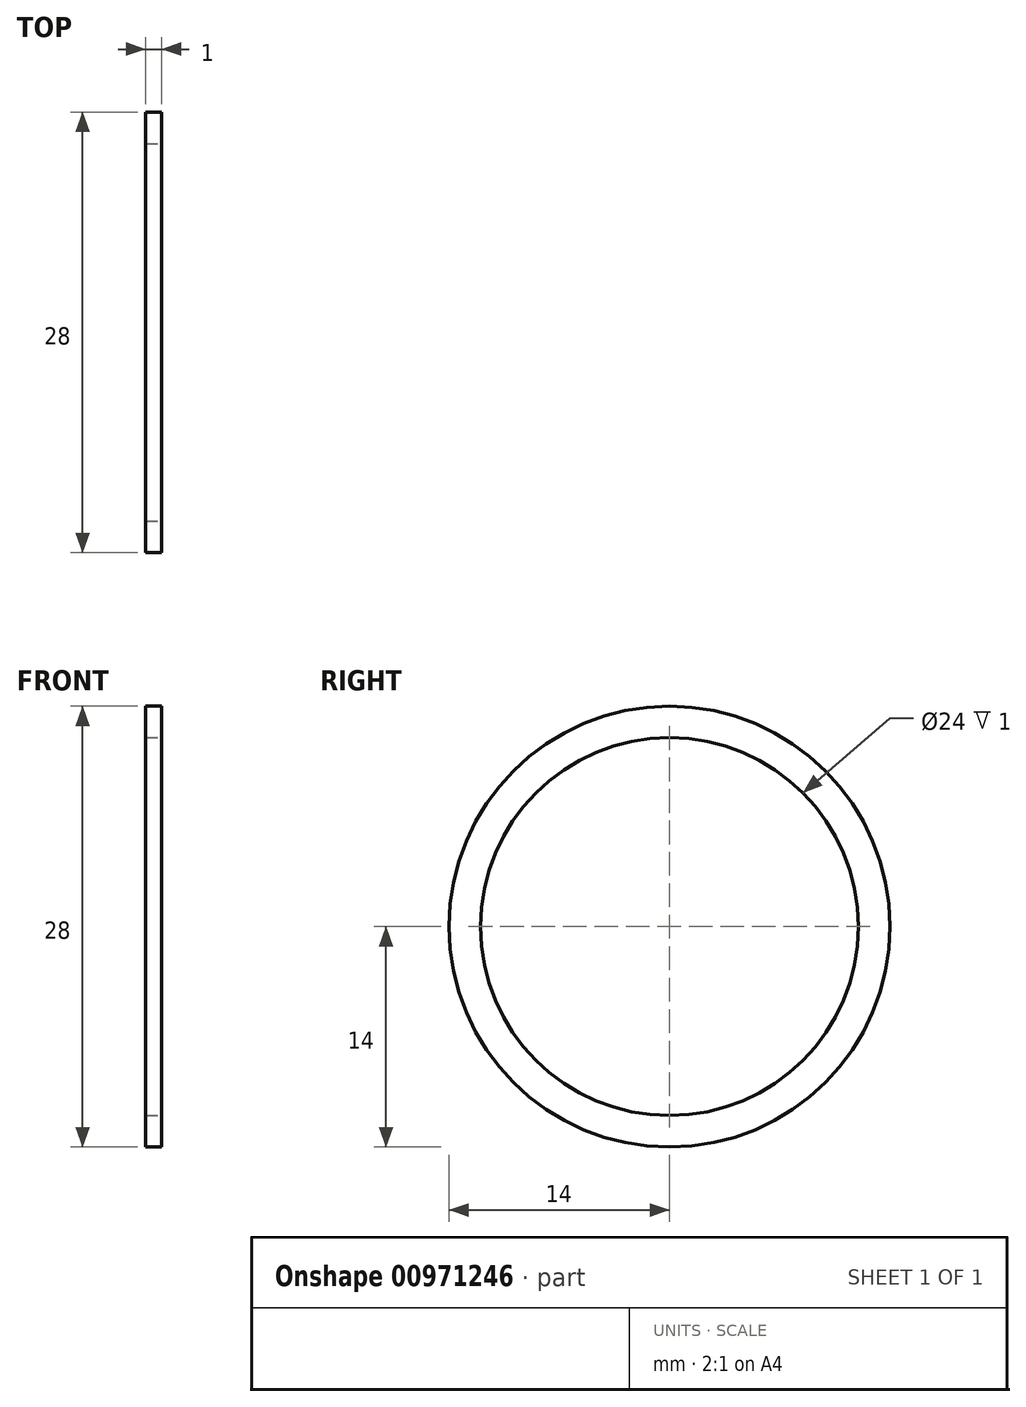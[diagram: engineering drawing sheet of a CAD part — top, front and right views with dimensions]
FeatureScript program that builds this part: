
annotation { "Feature Type Name" : "Feature", "Feature Type Description" : "" }
export const myFeature = defineFeature(function(context is Context, id is Id, definition is map)
    precondition{}
    {
        {
            var Q0;
            Q0=qCreatedBy(makeId("Front.planeOp"),FACE);
            var sketch = newSketch(context, id + "F0", { "sketchPlane" : qUnion([Q0])});
            skLineSegment(sketch, "E0.bottom", {"start": v(-14.02, 14) * mm, "end": v(-15.02, 14) * mm});
            skLineSegment(sketch, "E0.top", {"start": v(-14.02, 12) * mm, "end": v(-15.02, 12) * mm});
            skLineSegment(sketch, "E0.left", {"start": v(-14.02, 14) * mm, "end": v(-14.02, 12) * mm});
            skLineSegment(sketch, "E0.right", {"start": v(-15.02, 14) * mm, "end": v(-15.02, 12) * mm});
            skLineSegment(sketch, "E1", {"start": v(0, 0) * mm, "end": v(-14.12, 0) * mm});
            skSolve(sketch);
        }
        {
            var Q0;
            Q0=qSketchRegion(id+"F0",true);
            var Q1;
            Q1=sQuery(id+"F0.wireOp",EDGE,"E1");
            revolve(context, id + "F1", {"surfaceOperationType" : NewSurfaceOperationType.NEW, "entities" : qUnion([Q0]), "axis" : qUnion([Q1]), "revolveType" : RevolveType.FULL});
        }
    });
